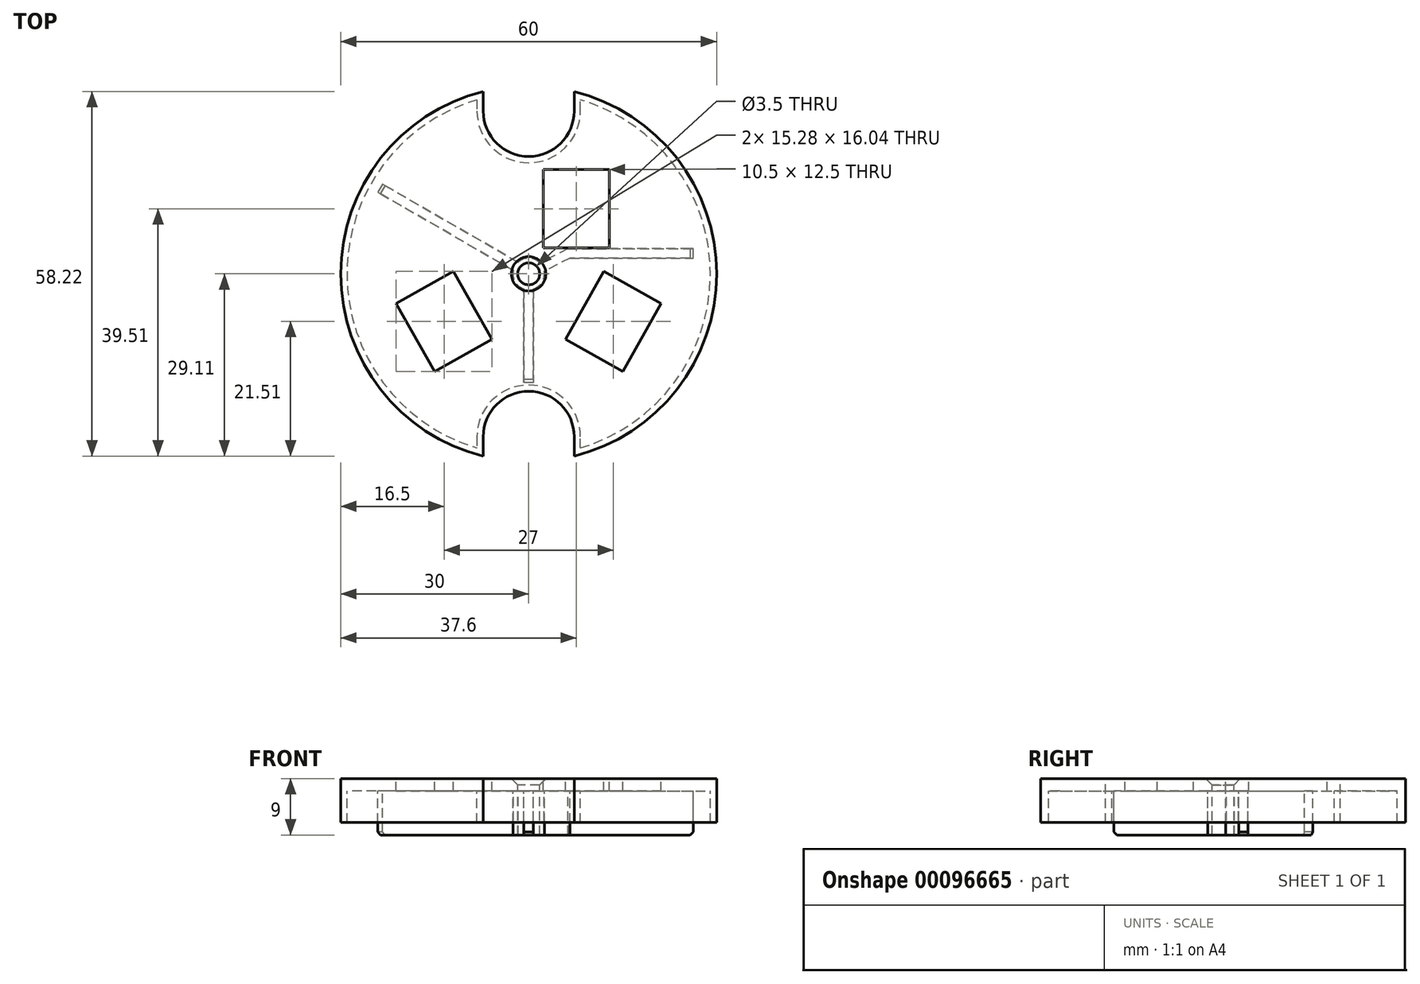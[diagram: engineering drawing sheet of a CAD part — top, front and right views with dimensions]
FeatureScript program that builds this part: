
annotation { "Feature Type Name" : "Feature", "Feature Type Description" : "" }
export const myFeature = defineFeature(function(context is Context, id is Id, definition is map)
    precondition{}
    {
        {
            var Q0;
            Q0=qCreatedBy(makeId("Top.planeOp"),FACE);
            var sketch = newSketch(context, id + "F0", { "sketchPlane" : qUnion([Q0])});
            skCircle(sketch, "E0", {"center": v(0, 0) * mm, "radius": 1.75 * mm});
            skCircle(sketch, "E1", {"center": v(0, 0) * mm, "radius": 2.5 * mm});
            skSolve(sketch);
        }
        {
            var Q0;
            Q0=qSketchRegion(id+"F0",true);
            extrude(context, id + "F1", {"entities" : qUnion([Q0]), "oppositeDirection" : true, "depth" : 7 * mm});
        }
        {
            var Q0;
            Q0=qCreatedBy(makeId("Top.planeOp"),FACE);
            var sketch = newSketch(context, id + "F2", { "sketchPlane" : qUnion([Q0])});
            skCircle(sketch, "E2", {"center": v(0, 0) * mm, "radius": 30 * mm});
            skCircle(sketch, "E3.0", {"center": v(0, 0) * mm, "radius": 1.75 * mm});
            skSolve(sketch);
        }
        {
            var Q0;
            Q0=qSketchRegion(id+"F2",true);
            extrude(context, id + "F3", {"entities" : qUnion([Q0]), "operationType" : NewBodyOperationType.ADD, "depth" : 2 * mm});
        }
        {
            var Q0;
            Q0=makeQuery(id+"F3.opExtrude","CAP_FACE",FACE,{"disambiguationData":[OSD([sQuery(id+"F2.wireOp",EDGE,"E2"),sQuery(id+"F2.wireOp",EDGE,"E3.0")])],"isStart":false});
            var sketch = newSketch(context, id + "F4", { "sketchPlane" : qUnion([Q0])});
            skLineSegment(sketch, "E4", {"start": v(0, 0) * mm, "end": v(7.6, 10.4) * mm, "construction": true});
            skLineSegment(sketch, "E5", {"start": v(0, 0) * mm, "end": v(13.5, -7.6) * mm, "construction": true});
            skPoint(sketch, "E6.middle", {"position": v(7.6, 10.4) * mm});
            skLineSegment(sketch, "E7.bottom", {"start": v(12.85, 4.15) * mm, "end": v(2.35, 4.15) * mm});
            skLineSegment(sketch, "E7.top", {"start": v(12.85, 16.65) * mm, "end": v(2.35, 16.65) * mm});
            skLineSegment(sketch, "E7.left", {"start": v(12.85, 4.15) * mm, "end": v(12.85, 16.65) * mm});
            skLineSegment(sketch, "E7.right", {"start": v(2.35, 4.15) * mm, "end": v(2.35, 16.65) * mm});
            skLineSegment(sketch, "E8.bottom", {"start": v(15, -15.62) * mm, "end": v(5.86, -10.47) * mm});
            skLineSegment(sketch, "E8.top", {"start": v(21.14, -4.73) * mm, "end": v(12, 0.42) * mm});
            skLineSegment(sketch, "E8.left", {"start": v(15, -15.62) * mm, "end": v(21.14, -4.73) * mm});
            skLineSegment(sketch, "E8.right", {"start": v(5.86, -10.47) * mm, "end": v(12, 0.42) * mm});
            skPoint(sketch, "E8.middle", {"position": v(13.5, -7.6) * mm});
            skLineSegment(sketch, "E9", {"start": v(0, 0) * mm, "end": v(0, -28.27) * mm, "construction": true});
            skLineSegment(sketch, "E10.MirrorCS", {"start": v(-5.86, -10.47) * mm, "end": v(-12, 0.42) * mm});
            skLineSegment(sketch, "E11.MirrorCS", {"start": v(-21.14, -4.73) * mm, "end": v(-12, 0.42) * mm});
            skLineSegment(sketch, "E12.MirrorCS", {"start": v(-15, -15.62) * mm, "end": v(-21.14, -4.73) * mm});
            skLineSegment(sketch, "E13.MirrorCS", {"start": v(-15, -15.62) * mm, "end": v(-5.86, -10.47) * mm});
            skSolve(sketch);
        }
        {
            var Q0;
            Q0=qSketchRegion(id+"F4",true);
            extrude(context, id + "F5", {"entities" : qUnion([Q0]), "operationType" : NewBodyOperationType.REMOVE, "endBound" : BoundingType.THROUGH_ALL, "oppositeDirection" : true, "depth" : 25 * mm});
        }
        {
            var Q0;
            Q0=makeQuery(id+"F3.opExtrude","CAP_FACE",FACE,{"disambiguationData":[OSD([sQuery(id+"F2.wireOp",EDGE,"E2"),sQuery(id+"F2.wireOp",EDGE,"E3.0")])],"isStart":false});
            var sketch = newSketch(context, id + "F6", { "sketchPlane" : qUnion([Q0])});
            skArc(sketch, "E14", {"start": v(-7.25, 26) * mm, "mid": v(0, 18.75) * mm, "end": v(7.25, 26) * mm});
            skArc(sketch, "E15.0", {"start": v(7.25, 29.11) * mm, "mid": v(0, 30) * mm, "end": v(-7.25, 29.11) * mm});
            skLineSegment(sketch, "E16", {"start": v(-7.25, 26) * mm, "end": v(-7.25, 29.11) * mm});
            skLineSegment(sketch, "E17", {"start": v(7.25, 26) * mm, "end": v(7.25, 29.11) * mm});
            skLineSegment(sketch, "E18", {"start": v(0, 0) * mm, "end": v(49.42, 0) * mm, "construction": true});
            skArc(sketch, "E19.MirrorCS", {"start": v(7.25, -29.11) * mm, "mid": v(0, -30) * mm, "end": v(-7.25, -29.11) * mm});
            skLineSegment(sketch, "E20.MirrorCS", {"start": v(-7.25, -26) * mm, "end": v(-7.25, -29.11) * mm});
            skArc(sketch, "E21.MirrorCS", {"start": v(-7.25, -26) * mm, "mid": v(0, -18.75) * mm, "end": v(7.25, -26) * mm});
            skLineSegment(sketch, "E22.MirrorCS", {"start": v(7.25, -26) * mm, "end": v(7.25, -29.11) * mm});
            skSolve(sketch);
        }
        {
            var Q0;
            Q0=qSketchRegion(id+"F6",true);
            extrude(context, id + "F7", {"entities" : qUnion([Q0]), "operationType" : NewBodyOperationType.REMOVE, "endBound" : BoundingType.THROUGH_ALL, "oppositeDirection" : true, "depth" : 25 * mm});
        }
        {
            var Q0;
            Q0=makeQuery(id+"F3.opExtrude","CAP_FACE",FACE,{"disambiguationData":[OSD([sQuery(id+"F2.wireOp",EDGE,"E2"),sQuery(id+"F2.wireOp",EDGE,"E3.0")])],"isStart":true});
            var sketch = newSketch(context, id + "F8", { "sketchPlane" : qUnion([Q0])});
            skLineSegment(sketch, "E23.bottom", {"start": v(6.24, -4.02) * mm, "end": v(1.78, -1.75) * mm});
            skLineSegment(sketch, "E23.top", {"start": v(6.6, -2.52) * mm, "end": v(2.47, -0.41) * mm});
            skLineSegment(sketch, "E23.right", {"start": v(1.78, -1.75) * mm, "end": v(2.47, -0.41) * mm});
            skLineSegment(sketch, "E24.bottom", {"start": v(0.75, 2.38) * mm, "end": v(-0.75, 2.38) * mm});
            skLineSegment(sketch, "E24.top", {"start": v(0.75, 17.38) * mm, "end": v(-0.75, 17.38) * mm});
            skLineSegment(sketch, "E24.left", {"start": v(0.75, 2.38) * mm, "end": v(0.75, 17.38) * mm});
            skLineSegment(sketch, "E24.right", {"start": v(-0.75, 2.38) * mm, "end": v(-0.75, 17.38) * mm});
            skLineSegment(sketch, "E25.bottom", {"start": v(-1.7, -1.84) * mm, "end": v(-23.34, -14.34) * mm});
            skLineSegment(sketch, "E25.top", {"start": v(-2.44, -0.54) * mm, "end": v(-24.1, -13.04) * mm});
            skLineSegment(sketch, "E25.left", {"start": v(-1.7, -1.84) * mm, "end": v(-2.44, -0.54) * mm});
            skLineSegment(sketch, "E25.right", {"start": v(-23.34, -14.34) * mm, "end": v(-24.1, -13.04) * mm});
            skLineSegment(sketch, "E26.bottom", {"start": v(6.6, -2.52) * mm, "end": v(26.24, -2.52) * mm});
            skLineSegment(sketch, "E26.top", {"start": v(6.24, -4.02) * mm, "end": v(26.24, -4.02) * mm});
            skLineSegment(sketch, "E26.right", {"start": v(26.24, -2.52) * mm, "end": v(26.24, -4.02) * mm});
            skSolve(sketch);
        }
        {
            var Q0;
            Q0=qSketchRegion(id+"F8",true);
            var Q1;
            Q1=makeQuery(id+"F1.opExtrude","CAP_FACE",FACE,{"disambiguationData":[OSD([sQuery(id+"F0.wireOp",EDGE,"E0"),sQuery(id+"F0.wireOp",EDGE,"E1")])],"isStart":false});
            extrude(context, id + "F9", {"entities" : qUnion([Q0]), "operationType" : NewBodyOperationType.ADD, "endBound" : BoundingType.UP_TO_SURFACE, "endBoundEntityFace" : qUnion([Q1]), "depth" : 10 * mm});
        }
        {
            var Q0;
            Q0=makeQuery(id+"F9.opExtrude","CAP_EDGE",EDGE,{"disambiguationData":[OSD([sQuery(id+"F8.wireOp",EDGE,"E25.bottom")])],"isStart":true});
            var Q1;
            {var subQ0=sQuery(id+"F0.wireOp",EDGE,"E1");Q1=makeQuery(id+"F9.boolean.opBoolean","SPLIT",EDGE,{"disambiguationData":[TD([makeQuery(id+"F9.opExtrude","SWEPT_FACE",FACE,{"disambiguationData":[OSD([sQuery(id+"F8.wireOp",EDGE,"E23.bottom")])]})])],"derivedFrom":makeQuery(id+"F1.opExtrude","CAP_EDGE",EDGE,{"disambiguationData":[OSD([subQ0])],"isStart":true})});}
            var Q2;
            Q2=makeQuery(id+"F9.opExtrude","CAP_EDGE",EDGE,{"disambiguationData":[OSD([sQuery(id+"F8.wireOp",EDGE,"E23.bottom")])],"isStart":true});
            var Q3;
            Q3=makeQuery(id+"F9.opExtrude","CAP_EDGE",EDGE,{"disambiguationData":[OSD([sQuery(id+"F8.wireOp",EDGE,"E26.top")])],"isStart":true});
            var Q4;
            Q4=makeQuery(id+"F9.opExtrude","CAP_EDGE",EDGE,{"disambiguationData":[OSD([sQuery(id+"F8.wireOp",EDGE,"E25.right")])],"isStart":true});
            var Q5;
            Q5=makeQuery(id+"F9.opExtrude","CAP_EDGE",EDGE,{"disambiguationData":[OSD([sQuery(id+"F8.wireOp",EDGE,"E26.right")])],"isStart":true});
            var Q6;
            Q6=makeQuery(id+"F9.opExtrude","CAP_EDGE",EDGE,{"disambiguationData":[OSD([sQuery(id+"F8.wireOp",EDGE,"E26.bottom")])],"isStart":true});
            var Q7;
            Q7=makeQuery(id+"F9.opExtrude","CAP_EDGE",EDGE,{"disambiguationData":[OSD([sQuery(id+"F8.wireOp",EDGE,"E23.top")])],"isStart":true});
            var Q8;
            {var subQ0=sQuery(id+"F0.wireOp",EDGE,"E1");Q8=makeQuery(id+"F9.boolean.opBoolean","SPLIT",EDGE,{"disambiguationData":[TD([makeQuery(id+"F9.opExtrude","SWEPT_FACE",FACE,{"disambiguationData":[OSD([sQuery(id+"F8.wireOp",EDGE,"E23.top")])]})])],"derivedFrom":makeQuery(id+"F1.opExtrude","CAP_EDGE",EDGE,{"disambiguationData":[OSD([subQ0])],"isStart":true})});}
            var Q9;
            Q9=makeQuery(id+"F9.opExtrude","CAP_EDGE",EDGE,{"disambiguationData":[OSD([sQuery(id+"F8.wireOp",EDGE,"E24.left")])],"isStart":true});
            var Q10;
            Q10=makeQuery(id+"F9.opExtrude","CAP_EDGE",EDGE,{"disambiguationData":[OSD([sQuery(id+"F8.wireOp",EDGE,"E24.top")])],"isStart":true});
            var Q11;
            Q11=makeQuery(id+"F9.opExtrude","CAP_EDGE",EDGE,{"disambiguationData":[OSD([sQuery(id+"F8.wireOp",EDGE,"E24.right")])],"isStart":true});
            var Q12;
            {var subQ0=sQuery(id+"F0.wireOp",EDGE,"E1");Q12=makeQuery(id+"F9.boolean.opBoolean","SPLIT",EDGE,{"disambiguationData":[TD([makeQuery(id+"F9.opExtrude","SWEPT_FACE",FACE,{"disambiguationData":[OSD([sQuery(id+"F8.wireOp",EDGE,"E24.right")])]})])],"derivedFrom":makeQuery(id+"F1.opExtrude","CAP_EDGE",EDGE,{"disambiguationData":[OSD([subQ0])],"isStart":true})});}
            var Q13;
            Q13=makeQuery(id+"F9.opExtrude","CAP_EDGE",EDGE,{"disambiguationData":[OSD([sQuery(id+"F8.wireOp",EDGE,"E25.top")])],"isStart":true});
            var Q14;
            Q14=makeQuery(id+"F9.opExtrude","CAP_EDGE",EDGE,{"disambiguationData":[OSD([sQuery(id+"F8.wireOp",EDGE,"E24.top")])],"isStart":false});
            var Q15;
            Q15=makeQuery(id+"F9.opExtrude","CAP_EDGE",EDGE,{"disambiguationData":[OSD([sQuery(id+"F8.wireOp",EDGE,"E25.right")])],"isStart":false});
            var Q16;
            Q16=makeQuery(id+"F9.opExtrude","CAP_EDGE",EDGE,{"disambiguationData":[OSD([sQuery(id+"F8.wireOp",EDGE,"E26.right")])],"isStart":false});
            chamfer(context, id + "F10", {"entities" : qUnion([Q0, Q1, Q2, Q3, Q4, Q5, Q6, Q7, Q8, Q9, Q10, Q11, Q12, Q13, Q14, Q15, Q16]), "width" : 0.5 * mm, "tangentPropagation" : true});
        }
        {
            var Q0;
            Q0=makeQuery(id+"F3.opExtrude","CAP_EDGE",EDGE,{"disambiguationData":[OSD([sQuery(id+"F2.wireOp",EDGE,"E3.0")])],"isStart":false});
            chamfer(context, id + "F11", {"entities" : qUnion([Q0]), "chamferType" : ChamferType.OFFSET_ANGLE, "width" : 1 * mm, "oppositeDirection" : false, "angle" : 45 * degree, "tangentPropagation" : true});
        }
        {
            var Q0;
            Q0=makeQuery(id+"F3.opExtrude","CAP_FACE",FACE,{"disambiguationData":[OSD([sQuery(id+"F2.wireOp",EDGE,"E2"),sQuery(id+"F2.wireOp",EDGE,"E3.0")])],"isStart":true});
            var sketch = newSketch(context, id + "F12", { "sketchPlane" : qUnion([Q0])});
            skArc(sketch, "E27.0", {"start": v(-7.25, -29.11) * mm, "mid": v(-30, 0) * mm, "end": v(-7.25, 29.11) * mm});
            skLineSegment(sketch, "E27.1", {"start": v(-7.25, 26) * mm, "end": v(-7.25, 29.11) * mm});
            skArc(sketch, "E27.2", {"start": v(-7.25, 26) * mm, "mid": v(0, 18.75) * mm, "end": v(7.25, 26) * mm});
            skArc(sketch, "E27.3", {"start": v(7.25, 29.11) * mm, "mid": v(30, 0) * mm, "end": v(7.25, -29.11) * mm});
            skLineSegment(sketch, "E27.4", {"start": v(7.25, 26) * mm, "end": v(7.25, 29.11) * mm});
            skLineSegment(sketch, "E27.5", {"start": v(7.25, -26) * mm, "end": v(7.25, -29.11) * mm});
            skArc(sketch, "E27.6", {"start": v(-7.25, -26) * mm, "mid": v(0, -18.75) * mm, "end": v(7.25, -26) * mm});
            skLineSegment(sketch, "E27.7", {"start": v(-7.25, -26) * mm, "end": v(-7.25, -29.11) * mm});
            skLineSegment(sketch, "E28.0", {"start": v(-8.25, 26) * mm, "end": v(-8.25, 27.8) * mm});
            skArc(sketch, "E28.1", {"start": v(-8.25, 27.8) * mm, "mid": v(-29, 0) * mm, "end": v(-8.25, -27.8) * mm});
            skArc(sketch, "E28.2", {"start": v(-8.25, 26) * mm, "mid": v(0, 17.75) * mm, "end": v(8.25, 26) * mm});
            skLineSegment(sketch, "E28.3", {"start": v(-8.25, -27.8) * mm, "end": v(-8.25, -26) * mm});
            skLineSegment(sketch, "E28.4", {"start": v(8.25, 27.8) * mm, "end": v(8.25, 26) * mm});
            skArc(sketch, "E28.5", {"start": v(8.25, -27.8) * mm, "mid": v(29, 0) * mm, "end": v(8.25, 27.8) * mm});
            skLineSegment(sketch, "E28.6", {"start": v(8.25, -26) * mm, "end": v(8.25, -27.8) * mm});
            skArc(sketch, "E28.7", {"start": v(-8.25, -26) * mm, "mid": v(0, -17.75) * mm, "end": v(8.25, -26) * mm});
            skSolve(sketch);
        }
        {
            var Q0;
            Q0=makeQuery(id+"F12.imprint","IMPRINT",FACE,{"disambiguationData":[TD([[makeQuery(id+"F12.imprint","IMPRINT",EDGE,{"derivedFrom":sQuery(id+"F12.wireOp",EDGE,"E27.0")}),-1.0]])]});
            extrude(context, id + "F13", {"entities" : qUnion([Q0]), "operationType" : NewBodyOperationType.ADD, "depth" : 5 * mm});
        }
    });
